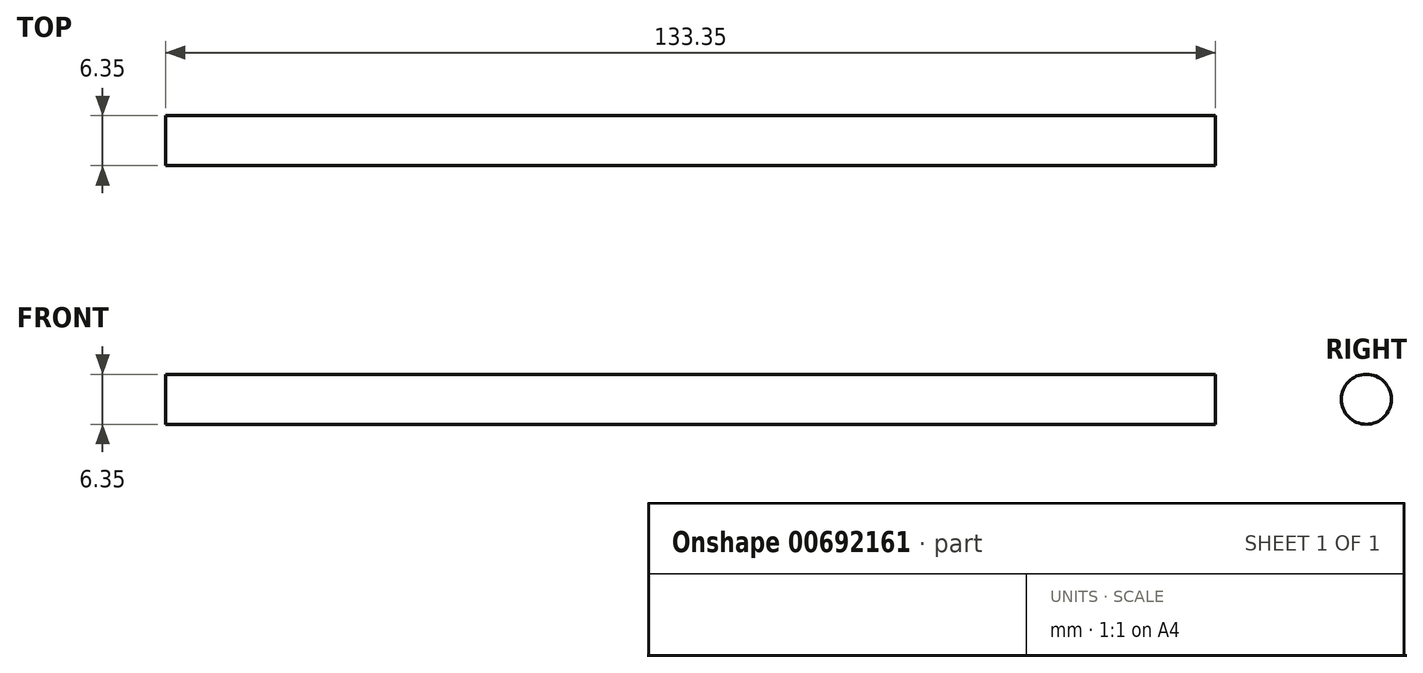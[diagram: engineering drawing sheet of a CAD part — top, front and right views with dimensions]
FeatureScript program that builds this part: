
annotation { "Feature Type Name" : "Feature", "Feature Type Description" : "" }
export const myFeature = defineFeature(function(context is Context, id is Id, definition is map)
    precondition{}
    {
        {
            var Q0;
            Q0=qCreatedBy(makeId("Right.planeOp"),FACE);
            var sketch = newSketch(context, id + "F0", { "sketchPlane" : qUnion([Q0])});
            skCircle(sketch, "E0", {"center": v(-34.97, 26.33) * mm, "radius": 3.18 * mm});
            skSolve(sketch);
        }
        {
            var Q0;
            Q0=makeQuery(id+"F0.imprint","IMPRINT",FACE,{"disambiguationData":[TD([[makeQuery(id+"F0.imprint","IMPRINT",EDGE,{"derivedFrom":sQuery(id+"F0.wireOp",EDGE,"E0")}),1.0]])]});
            extrude(context, id + "F1", {"entities" : qUnion([Q0]), "depth" : 133.35 * mm, "offsetDistance" : 25.4 * mm});
        }
    });
